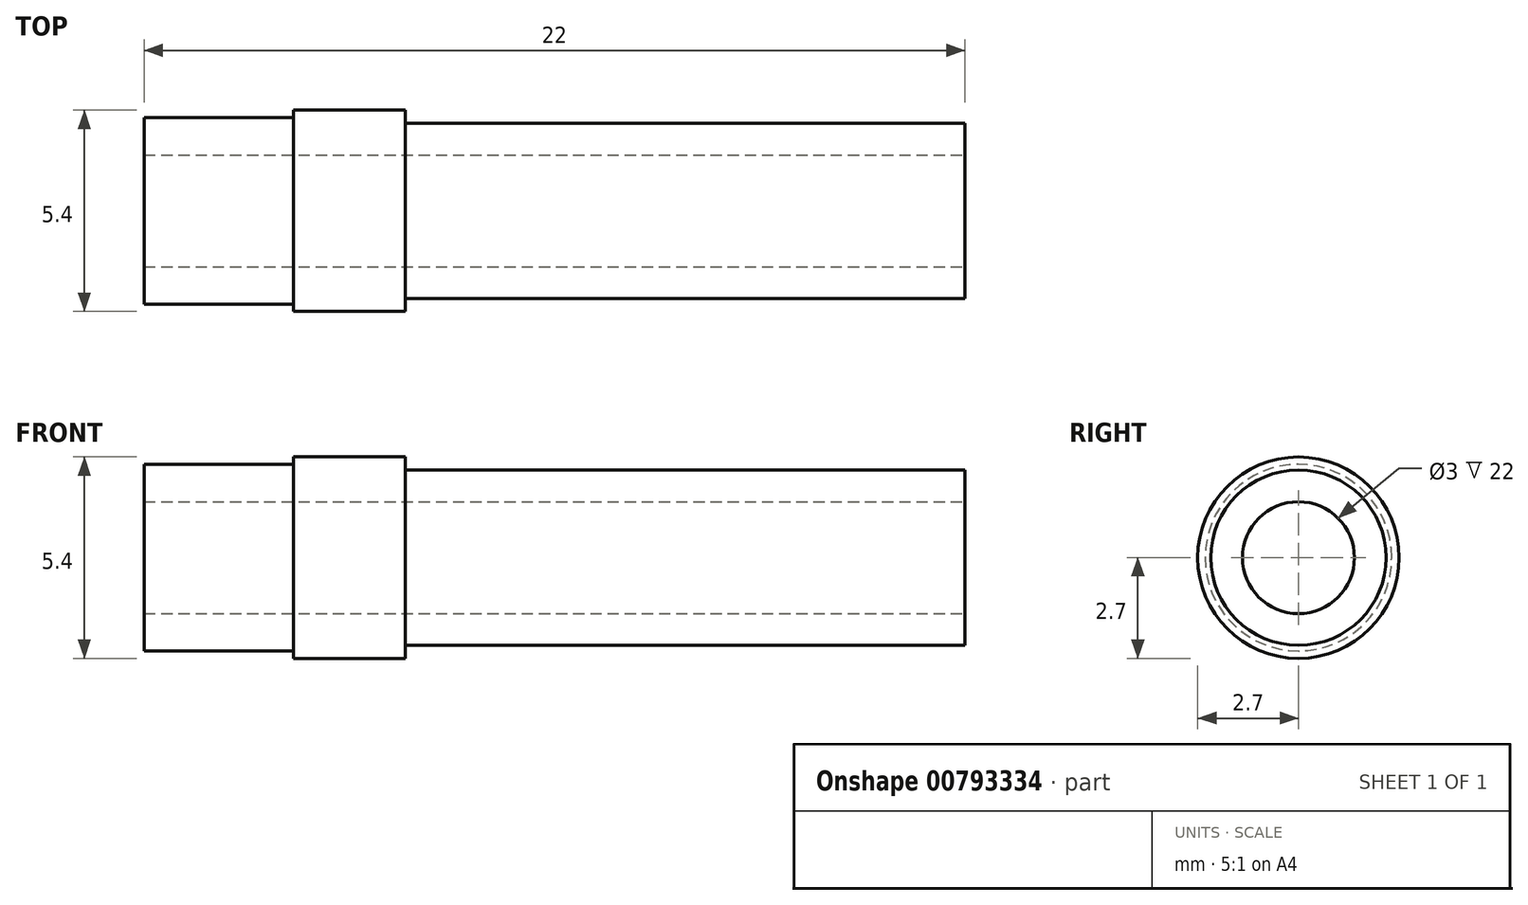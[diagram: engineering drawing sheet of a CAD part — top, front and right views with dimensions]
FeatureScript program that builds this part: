
annotation { "Feature Type Name" : "Feature", "Feature Type Description" : "" }
export const myFeature = defineFeature(function(context is Context, id is Id, definition is map)
    precondition{}
    {
        {
            var Q0;
            Q0=qCreatedBy(makeId("Front.planeOp"),FACE);
            var sketch = newSketch(context, id + "F0", { "sketchPlane" : qUnion([Q0])});
            skLineSegment(sketch, "E0", {"start": v(-3.04, 2.7) * mm, "end": v(-0.04, 2.7) * mm});
            skLineSegment(sketch, "E1", {"start": v(-0.04, 2.7) * mm, "end": v(-0.04, 2.35) * mm});
            skLineSegment(sketch, "E2", {"start": v(-0.04, 2.35) * mm, "end": v(14.96, 2.35) * mm});
            skLineSegment(sketch, "E3", {"start": v(14.96, 2.35) * mm, "end": v(14.96, 0) * mm});
            skLineSegment(sketch, "E4", {"start": v(14.96, 0) * mm, "end": v(-7.04, 0) * mm});
            skLineSegment(sketch, "E5", {"start": v(-3.04, 2.7) * mm, "end": v(-3.04, 2.5) * mm});
            skLineSegment(sketch, "E6", {"start": v(-3.04, 2.5) * mm, "end": v(-7.04, 2.5) * mm});
            skLineSegment(sketch, "E7", {"start": v(-7.04, 2.5) * mm, "end": v(-7.04, 0) * mm});
            skSolve(sketch);
        }
        {
            var Q0;
            Q0=makeQuery(id+"F0.imprint","IMPRINT",FACE,{"disambiguationData":[TD([[makeQuery(id+"F0.imprint","IMPRINT",EDGE,{"derivedFrom":sQuery(id+"F0.wireOp",EDGE,"E0")}),-1.0]])]});
            var Q1;
            Q1=sQuery(id+"F0.wireOp",EDGE,"E4");
            revolve(context, id + "F1", {"entities" : qUnion([Q0]), "axis" : qUnion([Q1]), "revolveType" : RevolveType.FULL});
        }
        {
            var Q0;
            Q0=makeQuery(id+"F1.opRevolve","SWEPT_FACE",FACE,{"disambiguationData":[OSD([sQuery(id+"F0.wireOp",EDGE,"E3")])]});
            var sketch = newSketch(context, id + "F2", { "sketchPlane" : qUnion([Q0])});
            skCircle(sketch, "E8", {"center": v(0, 0) * mm, "radius": 1.5 * mm});
            skSolve(sketch);
        }
        {
            var Q0;
            Q0=qSketchRegion(id+"F2",true);
            extrude(context, id + "F3", {"entities" : qUnion([Q0]), "operationType" : NewBodyOperationType.REMOVE, "oppositeDirection" : true, "depth" : 25 * mm, "offsetDistance" : 25 * mm});
        }
    });
